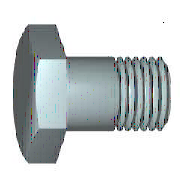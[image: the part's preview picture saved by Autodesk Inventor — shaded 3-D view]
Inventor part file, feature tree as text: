
AUTODESK INVENTOR PART (.ipt)
format: ipt  version: 2025 (Build 290162000, 162)  size: 196,608 bytes
history: native  units: mm (DEFAULTED — no unit token found)
features: other x1, extrude x1, chamfer x1, plane x1
ambient origin geometry x7: Origin, YZ Plane, XZ Plane, X Axis, Y Axis, Z Axis, Center Point
bodies: Solid1 (feature_tree)
feature tree (4):
  other  "轴承体"
  extrude  "头"  Depth=25.0mm
  chamfer  "倒角1"  Distance=23.75mm
  plane  "Work Plane1"
